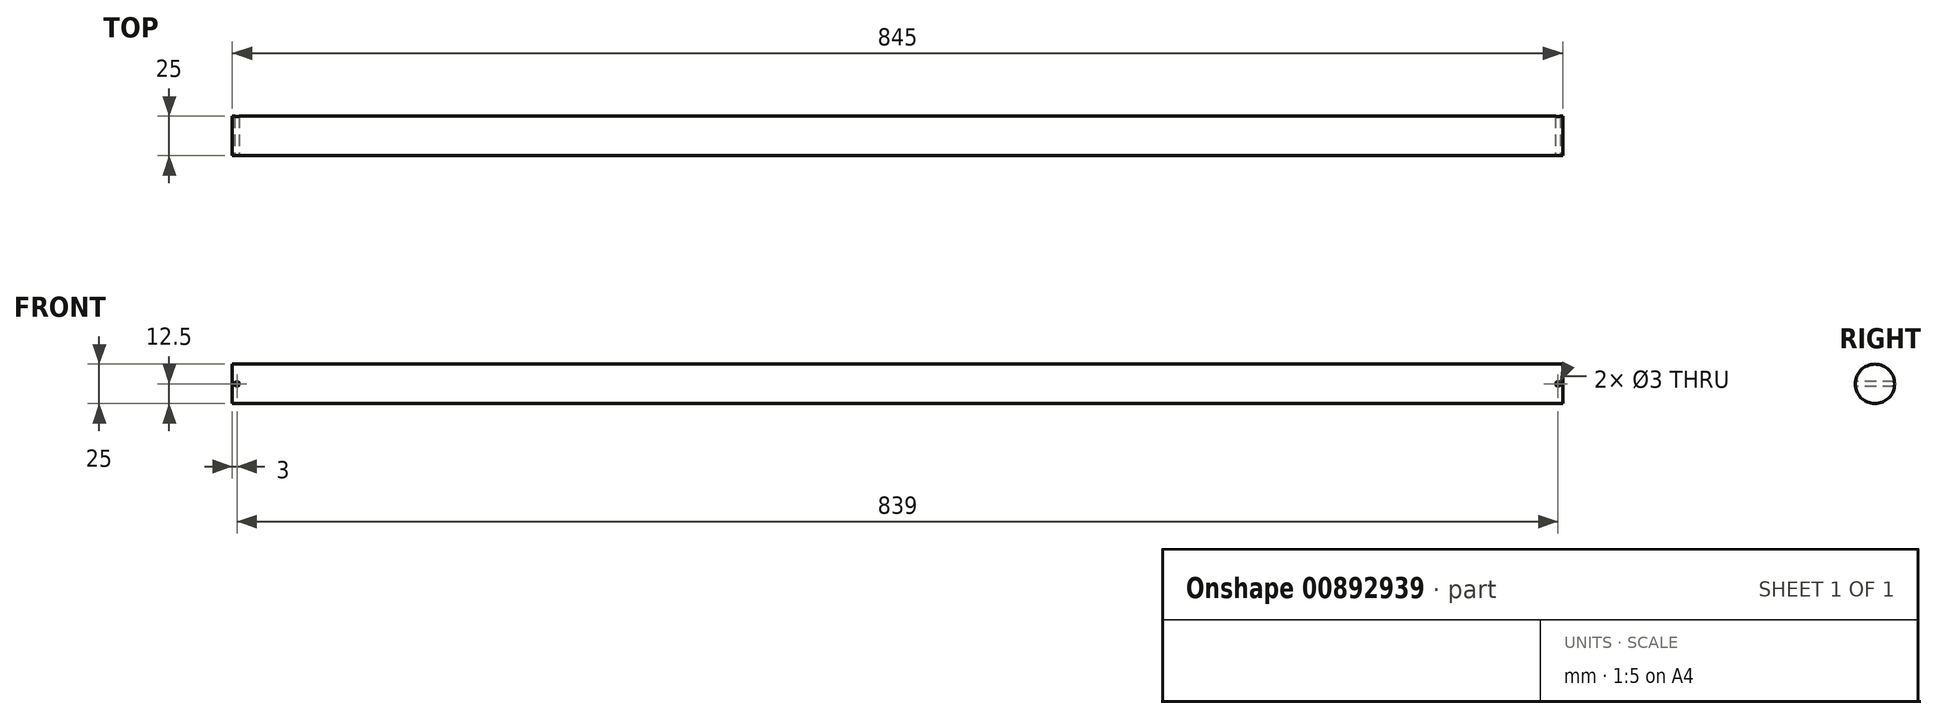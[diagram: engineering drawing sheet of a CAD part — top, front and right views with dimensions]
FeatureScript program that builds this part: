
annotation { "Feature Type Name" : "Feature", "Feature Type Description" : "" }
export const myFeature = defineFeature(function(context is Context, id is Id, definition is map)
    precondition{}
    {
        {
            var Q0;
            Q0=qCreatedBy(makeId("Right.planeOp"),FACE);
            var sketch = newSketch(context, id + "F0", { "sketchPlane" : qUnion([Q0])});
            skCircle(sketch, "E0", {"center": v(0, 0) * mm, "radius": 12.5 * mm});
            skSolve(sketch);
        }
        {
            var Q0;
            Q0=makeQuery(id+"F0.imprint","IMPRINT",FACE,{"disambiguationData":[TD([[makeQuery(id+"F0.imprint","IMPRINT",EDGE,{"derivedFrom":sQuery(id+"F0.wireOp",EDGE,"E0")}),1.0]])]});
            extrude(context, id + "F1", {"entities" : qUnion([Q0]), "endBound" : BoundingType.SYMMETRIC, "depth" : 845 * mm, "offsetDistance" : 25 * mm});
        }
        {
            var Q0;
            Q0=qCreatedBy(makeId("Front.planeOp"),FACE);
            var sketch = newSketch(context, id + "F2", { "sketchPlane" : qUnion([Q0])});
            skCircle(sketch, "E1", {"center": v(-419.5, 0) * mm, "radius": 1.5 * mm});
            skCircle(sketch, "E2.MirrorC", {"center": v(419.5, 0) * mm, "radius": 1.5 * mm});
            skSolve(sketch);
        }
        {
            var Q0;
            Q0 = qSketchRegion(id + "F2", true);
            extrude(context, id + "F3", {"entities" : qUnion([Q0]), "operationType" : NewBodyOperationType.REMOVE, "endBound" : BoundingType.THROUGH_ALL, "oppositeDirection" : true, "depth" : 25 * mm, "offsetDistance" : 25 * mm, "hasSecondDirection" : true, "secondDirectionBound" : SecondDirectionBoundingType.THROUGH_ALL, "secondDirectionOppositeDirection" : false, "secondDirectionDepth" : 25 * mm});
        }
    });
